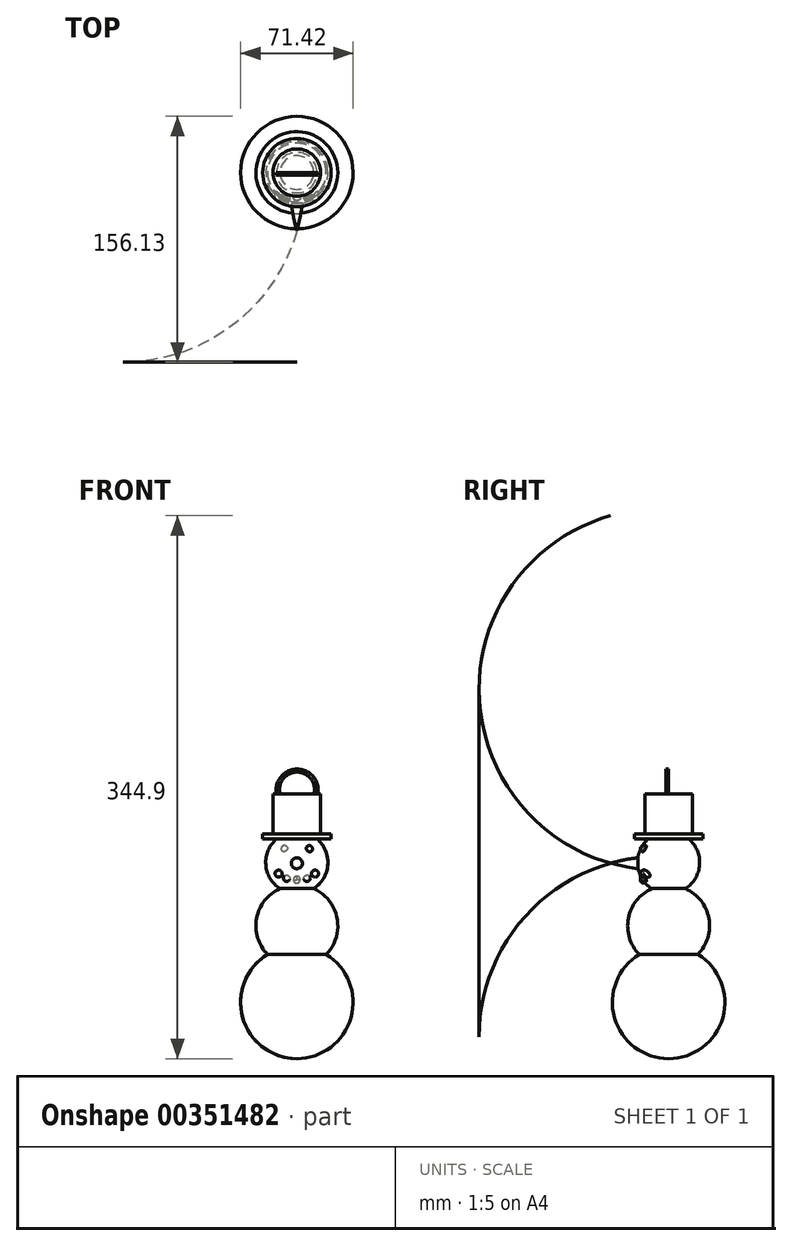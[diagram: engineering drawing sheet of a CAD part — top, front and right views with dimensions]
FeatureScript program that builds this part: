
annotation { "Feature Type Name" : "Feature", "Feature Type Description" : "" }
export const myFeature = defineFeature(function(context is Context, id is Id, definition is map)
    precondition{}
    {
        {
            var Q0;
            Q0=qCreatedBy(makeId("Front.planeOp"),FACE);
            var sketch = newSketch(context, id + "F0", { "sketchPlane" : qUnion([Q0])});
            skArc(sketch, "E0", {"start": v(0, -71.46) * mm, "mid": v(35.71, -35.75) * mm, "end": v(0, -0.04) * mm});
            skLineSegment(sketch, "E1", {"start": v(0, 0) * mm, "end": v(0, -71.46) * mm});
            skSolve(sketch);
        }
        {
            var Q0;
            Q0 = qSketchRegion(id + "F0", true);
            var Q1;
            Q1=sQuery(id+"F0.wireOp",EDGE,"E1");
            revolve(context, id + "F1", {"entities" : qUnion([Q0]), "axis" : qUnion([Q1]), "revolveType" : RevolveType.FULL});
        }
        {
            var Q0;
            Q0=qCreatedBy(makeId("Front.planeOp"),FACE);
            var sketch = newSketch(context, id + "F2", { "sketchPlane" : qUnion([Q0])});
            skArc(sketch, "E2", {"start": v(0, -13.15) * mm, "mid": v(26, 12.85) * mm, "end": v(0, 38.86) * mm});
            skLineSegment(sketch, "E3", {"start": v(0, 38.86) * mm, "end": v(0, -13.15) * mm});
            skSolve(sketch);
        }
        {
            var Q0;
            Q0 = qSketchRegion(id + "F2", true);
            var Q1;
            Q1=sQuery(id+"F2.wireOp",EDGE,"E3");
            revolve(context, id + "F3", {"operationType" : NewBodyOperationType.ADD, "entities" : qUnion([Q0]), "axis" : qUnion([Q1]), "revolveType" : RevolveType.FULL});
        }
        {
            var Q0;
            Q0=qCreatedBy(makeId("Front.planeOp"),FACE);
            var sketch = newSketch(context, id + "F4", { "sketchPlane" : qUnion([Q0])});
            skArc(sketch, "E4", {"start": v(0, 33.42) * mm, "mid": v(19.75, 53.16) * mm, "end": v(0, 72.9) * mm});
            skLineSegment(sketch, "E5", {"start": v(0, 72.9) * mm, "end": v(0, 33.42) * mm});
            skSolve(sketch);
        }
        {
            var Q0;
            Q0 = qSketchRegion(id + "F4", true);
            var Q1;
            Q1=sQuery(id+"F4.wireOp",EDGE,"E5");
            revolve(context, id + "F5", {"operationType" : NewBodyOperationType.ADD, "entities" : qUnion([Q0]), "axis" : qUnion([Q1]), "revolveType" : RevolveType.FULL});
        }
        {
            var Q0;
            Q0=qCreatedBy(makeId("Right.planeOp"),FACE);
            var sketch = newSketch(context, id + "F6", { "sketchPlane" : qUnion([Q0])});
            skLineSegment(sketch, "E6", {"start": v(0, 52.68) * mm, "end": v(-36.93, 52.68) * mm});
            skArc(sketch, "E7", {"start": v(-1.58, 56.93) * mm, "mid": v(-19.42, 56.19) * mm, "end": v(-36.93, 52.68) * mm});
            skLineSegment(sketch, "E8", {"start": v(0, 52.68) * mm, "end": v(-1.58, 56.93) * mm});
            skSolve(sketch);
        }
        {
            var Q0;
            Q0 = qSketchRegion(id + "F6", true);
            var Q1;
            Q1=sQuery(id+"F6.wireOp",EDGE,"E6");
            revolve(context, id + "F7", {"operationType" : NewBodyOperationType.ADD, "entities" : qUnion([Q0]), "axis" : qUnion([Q1]), "revolveType" : RevolveType.FULL});
        }
        {
            var Q0;
            Q0=qCreatedBy(makeId("Front.planeOp"),FACE);
            var sketch = newSketch(context, id + "F8", { "sketchPlane" : qUnion([Q0])});
            skCircle(sketch, "E9", {"center": v(7.9, 61.84) * mm, "radius": 2.06 * mm});
            skArc(sketch, "E10", {"start": v(0, 40.05) * mm, "mid": v(2.2, 42.24) * mm, "end": v(0, 44.43) * mm});
            skCircle(sketch, "E11", {"center": v(6.41, 43.26) * mm, "radius": 2.13 * mm});
            skCircle(sketch, "E12", {"center": v(11.57, 46.07) * mm, "radius": 2.25 * mm});
            skLineSegment(sketch, "E13", {"start": v(0, 44.43) * mm, "end": v(0, 40.05) * mm});
            skCircle(sketch, "E14.MirrorC", {"center": v(-6.41, 43.26) * mm, "radius": 2.13 * mm});
            skArc(sketch, "E15.MirrorCS", {"start": v(0, 40.05) * mm, "mid": v(-2.2, 42.24) * mm, "end": v(0, 44.43) * mm});
            skCircle(sketch, "E16.MirrorC", {"center": v(-11.57, 46.07) * mm, "radius": 2.25 * mm});
            skCircle(sketch, "E17.MirrorC", {"center": v(-7.9, 61.84) * mm, "radius": 2.06 * mm});
            skSolve(sketch);
        }
        {
            var Q0;
            Q0 = qSketchRegion(id + "F8", true);
            extrude(context, id + "F9", {"entities" : qUnion([Q0]), "operationType" : NewBodyOperationType.ADD, "depth" : 17.9 * mm});
        }
        {
            var Q0;
            Q0=makeQuery(id+"F9.opExtrude","CAP_EDGE",EDGE,{"disambiguationData":[OSD([sQuery(id+"F8.wireOp",EDGE,"E9")])],"isStart":false});
            var Q1;
            Q1=makeQuery(id+"F9.opExtrude","CAP_EDGE",EDGE,{"disambiguationData":[OSD([sQuery(id+"F8.wireOp",EDGE,"E17.MirrorC")])],"isStart":false});
            var Q2;
            Q2=makeQuery(id+"F9.opExtrude","CAP_EDGE",EDGE,{"disambiguationData":[OSD([sQuery(id+"F8.wireOp",EDGE,"E12")])],"isStart":false});
            var Q3;
            Q3=makeQuery(id+"F9.opExtrude","CAP_EDGE",EDGE,{"disambiguationData":[OSD([sQuery(id+"F8.wireOp",EDGE,"E11")])],"isStart":false});
            var Q4;
            Q4=makeQuery(id+"F9.opExtrude","CAP_EDGE",EDGE,{"disambiguationData":[OSD([sQuery(id+"F8.wireOp",EDGE,"E10"),sQuery(id+"F8.wireOp",EDGE,"E15.MirrorCS")])],"isStart":false});
            var Q5;
            Q5=makeQuery(id+"F9.opExtrude","CAP_EDGE",EDGE,{"disambiguationData":[OSD([sQuery(id+"F8.wireOp",EDGE,"E14.MirrorC")])],"isStart":false});
            var Q6;
            Q6=makeQuery(id+"F9.opExtrude","CAP_EDGE",EDGE,{"disambiguationData":[OSD([sQuery(id+"F8.wireOp",EDGE,"E16.MirrorC")])],"isStart":false});
            fillet(context, id + "F10", {"entities" : qUnion([Q0, Q1, Q2, Q3, Q4, Q5, Q6]), "radius" : 2.03 * mm, "tangentPropagation" : true, "allowEdgeOverflow" : false});
        }
        {
            var Q0;
            Q0=qCreatedBy(makeId("Front.planeOp"),FACE);
            var sketch = newSketch(context, id + "F11", { "sketchPlane" : qUnion([Q0])});
            skLineSegment(sketch, "E18", {"start": v(0, 68.16) * mm, "end": v(21.68, 68.16) * mm});
            skLineSegment(sketch, "E19", {"start": v(21.68, 68.16) * mm, "end": v(21.68, 71.18) * mm});
            skLineSegment(sketch, "E20", {"start": v(21.68, 71.18) * mm, "end": v(0, 71.18) * mm});
            skLineSegment(sketch, "E21", {"start": v(0, 71.18) * mm, "end": v(0, 68.16) * mm});
            skSolve(sketch);
        }
        {
            var Q0;
            Q0 = qSketchRegion(id + "F11", true);
            var Q1;
            Q1=sQuery(id+"F11.wireOp",EDGE,"E21");
            revolve(context, id + "F12", {"operationType" : NewBodyOperationType.ADD, "entities" : qUnion([Q0]), "axis" : qUnion([Q1]), "revolveType" : RevolveType.FULL});
        }
        {
            var Q0;
            Q0=makeQuery(id+"F12.opRevolve","SWEPT_FACE",FACE,{"disambiguationData":[OSD([sQuery(id+"F11.wireOp",EDGE,"E20")])]});
            var sketch = newSketch(context, id + "F13", { "sketchPlane" : qUnion([Q0])});
            skCircle(sketch, "E22", {"center": v(0, 0) * mm, "radius": 15.05 * mm});
            skSolve(sketch);
        }
        {
            var Q0;
            Q0 = qSketchRegion(id + "F13", true);
            extrude(context, id + "F14", {"entities" : qUnion([Q0]), "operationType" : NewBodyOperationType.ADD, "depth" : 25.4 * mm});
        }
        {
            var Q0;
            Q0=qCreatedBy(makeId("Front.planeOp"),FACE);
            var sketch = newSketch(context, id + "F15", { "sketchPlane" : qUnion([Q0])});
            skArc(sketch, "E23", {"start": v(13.18, 95.84) * mm, "mid": v(0.38, 112.47) * mm, "end": v(-12.91, 96.23) * mm});
            skArc(sketch, "E24", {"start": v(10.74, 96.2) * mm, "mid": v(0.03, 110.6) * mm, "end": v(-10.4, 95.99) * mm});
            skLineSegment(sketch, "E25", {"start": v(10.74, 96.2) * mm, "end": v(13.18, 95.84) * mm});
            skLineSegment(sketch, "E26", {"start": v(-10.4, 95.99) * mm, "end": v(-12.91, 96.23) * mm});
            skSolve(sketch);
        }
        {
            var Q0;
            Q0 = qSketchRegion(id + "F15", true);
            extrude(context, id + "F16", {"entities" : qUnion([Q0]), "operationType" : NewBodyOperationType.ADD, "depth" : 1.61 * mm});
        }
    });
